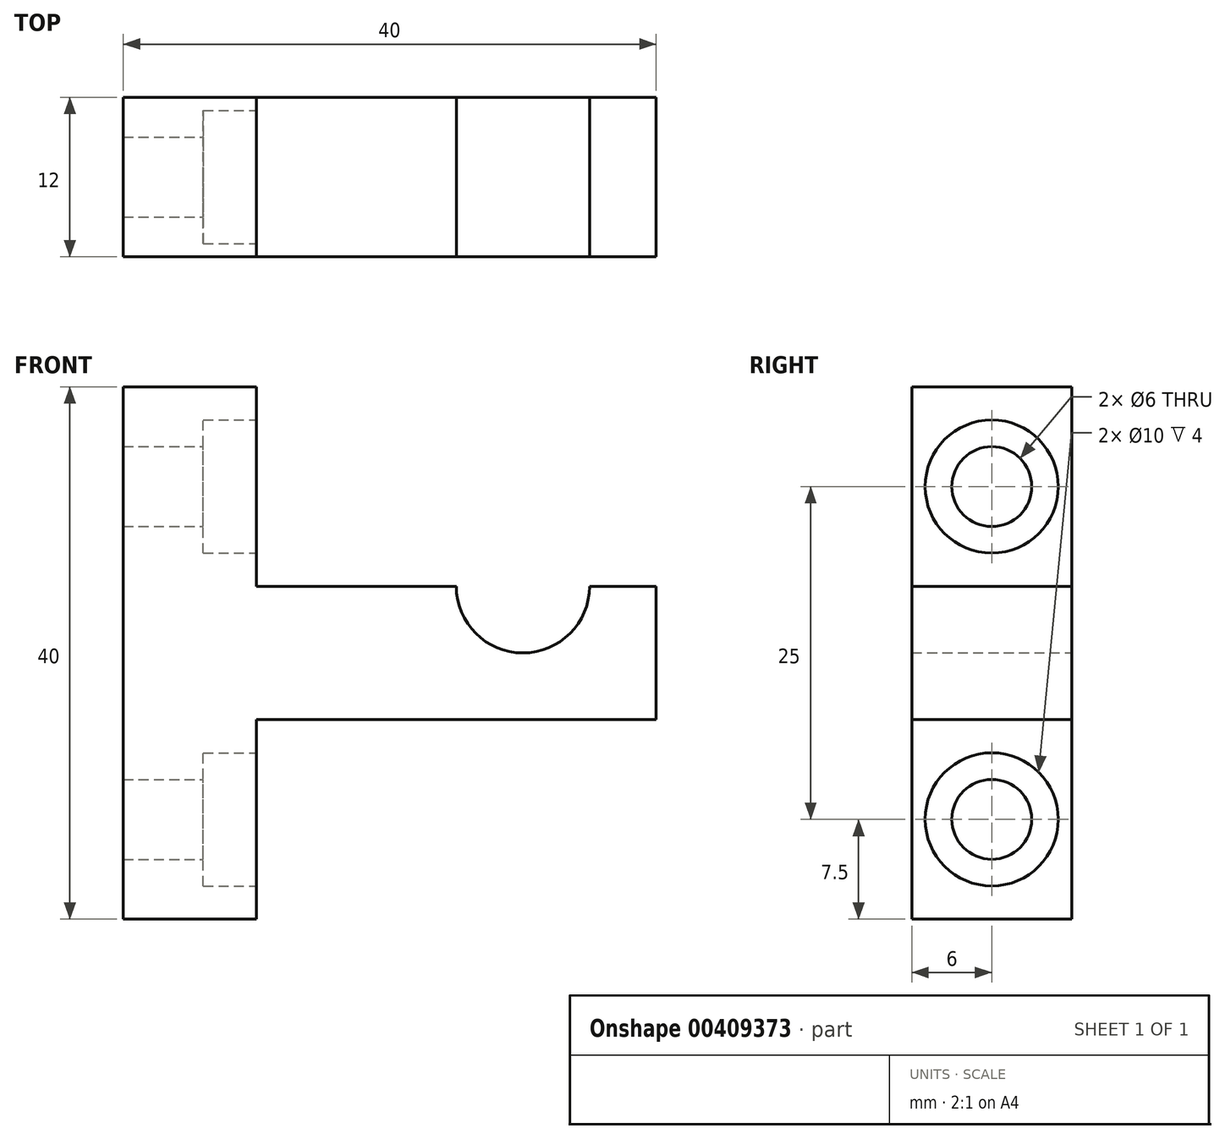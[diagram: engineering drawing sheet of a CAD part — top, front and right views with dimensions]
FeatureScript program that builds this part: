
annotation { "Feature Type Name" : "Feature", "Feature Type Description" : "" }
export const myFeature = defineFeature(function(context is Context, id is Id, definition is map)
    precondition{}
    {
        {
            var Q0;
            Q0=qCreatedBy(makeId("Front.planeOp"),FACE);
            var sketch = newSketch(context, id + "F0", { "sketchPlane" : qUnion([Q0])});
            skLineSegment(sketch, "E0.bottom", {"start": v(20, -20) * mm, "end": v(-20, -20) * mm});
            skLineSegment(sketch, "E0.top", {"start": v(20, 20) * mm, "end": v(-20, 20) * mm});
            skLineSegment(sketch, "E0.left", {"start": v(20, -20) * mm, "end": v(20, 20) * mm});
            skLineSegment(sketch, "E0.right", {"start": v(-20, -20) * mm, "end": v(-20, 20) * mm});
            skPoint(sketch, "E0.middle", {"position": v(0, 0) * mm});
            skPoint(sketch, "E1", {"position": v(10, 5) * mm});
            skCircle(sketch, "E2", {"center": v(10, 5) * mm, "radius": 5 * mm});
            skLineSegment(sketch, "E3", {"start": v(-20, 5) * mm, "end": v(20, 5) * mm});
            skLineSegment(sketch, "E4", {"start": v(-20, -5) * mm, "end": v(20, -5) * mm});
            skLineSegment(sketch, "E5", {"start": v(-10, 20) * mm, "end": v(-10, -20) * mm});
            skSolve(sketch);
        }
        {
            var Q0;
            {var subQ0=sQuery(id+"F0.wireOp",EDGE,"E0.right");var subQ1=sQuery(id+"F0.wireOp",EDGE,"E0.top");var subQ2=makeQuery(id+"F0.imprint","INTERSECT",VERTEX,{"derivedFrom":[subQ1,subQ0]});Q0=makeQuery(id+"F0.imprint","IMPRINT",FACE,{"disambiguationData":[TD([[makeQuery(id+"F0.imprint","IMPRINT",EDGE,{"disambiguationData":[TD([[subQ2,1.0]])],"derivedFrom":subQ1}),1.0]])]});}
            var Q1;
            {var subQ0=sQuery(id+"F0.wireOp",EDGE,"E3");var subQ1=sQuery(id+"F0.wireOp",EDGE,"E0.right");var subQ2=makeQuery(id+"F0.imprint","INTERSECT",VERTEX,{"derivedFrom":[subQ1,subQ0]});Q1=makeQuery(id+"F0.imprint","IMPRINT",FACE,{"disambiguationData":[TD([[makeQuery(id+"F0.imprint","IMPRINT",EDGE,{"disambiguationData":[TD([[subQ2,1.0]])],"derivedFrom":subQ1}),-1.0]])]});}
            var Q2;
            {var subQ0=sQuery(id+"F0.wireOp",EDGE,"E0.right");var subQ1=sQuery(id+"F0.wireOp",EDGE,"E0.bottom");var subQ2=makeQuery(id+"F0.imprint","INTERSECT",VERTEX,{"derivedFrom":[subQ1,subQ0]});Q2=makeQuery(id+"F0.imprint","IMPRINT",FACE,{"disambiguationData":[TD([[makeQuery(id+"F0.imprint","IMPRINT",EDGE,{"disambiguationData":[TD([[subQ2,1.0]])],"derivedFrom":subQ1}),-1.0]])]});}
            var Q3;
            {var subQ0=sQuery(id+"F0.wireOp",EDGE,"E3");var subQ6=sQuery(id+"F0.wireOp",EDGE,"E0.left");var subQ7=makeQuery(id+"F0.imprint","INTERSECT",VERTEX,{"derivedFrom":[subQ6,subQ0]});Q3=makeQuery(id+"F0.imprint","IMPRINT",FACE,{"disambiguationData":[TD([[makeQuery(id+"F0.imprint","IMPRINT",EDGE,{"disambiguationData":[TD([[subQ7,1.0]])],"derivedFrom":subQ6}),1.0]])]});}
            extrude(context, id + "F1", {"entities" : qUnion([Q0, Q1, Q2, Q3]), "depth" : 12 * mm});
        }
        {
            var Q0;
            {var subQ0=sQuery(id+"F0.wireOp",EDGE,"E5");Q0=makeQuery(id+"F1.opExtrude","SWEPT_FACE",FACE,{"disambiguationData":[OSD([subQ0]),TDD([makeQuery(id+"F0.imprint","IMPRINT",EDGE,{"disambiguationData":[TD([[makeQuery(id+"F0.imprint","INTERSECT",VERTEX,{"derivedFrom":[sQuery(id+"F0.wireOp",EDGE,"E0.top"),subQ0]}),-1.0]])],"derivedFrom":subQ0})])]});}
            var sketch = newSketch(context, id + "F2", { "sketchPlane" : qUnion([Q0])});
            skPoint(sketch, "E6", {"position": v(-6, 12.5) * mm});
            skPoint(sketch, "E6.positionSnap0", {"position": v(-6, 5) * mm});
            skPoint(sketch, "E7", {"position": v(-6, -12.5) * mm});
            skCircle(sketch, "E8", {"center": v(-6, 12.5) * mm, "radius": 3 * mm});
            skCircle(sketch, "E9", {"center": v(-6, -12.5) * mm, "radius": 3 * mm});
            skSolve(sketch);
        }
        {
            var Q0;
            Q0=makeQuery(id+"F2.imprint","IMPRINT",FACE,{"disambiguationData":[TD([[makeQuery(id+"F2.imprint","IMPRINT",EDGE,{"derivedFrom":sQuery(id+"F2.wireOp",EDGE,"E8")}),1.0]])]});
            var Q1;
            Q1=makeQuery(id+"F2.imprint","IMPRINT",FACE,{"disambiguationData":[TD([[makeQuery(id+"F2.imprint","IMPRINT",EDGE,{"derivedFrom":sQuery(id+"F2.wireOp",EDGE,"E9")}),1.0]])]});
            extrude(context, id + "F3", {"entities" : qUnion([Q0, Q1]), "operationType" : NewBodyOperationType.REMOVE, "endBound" : BoundingType.THROUGH_ALL, "oppositeDirection" : true, "depth" : 25 * mm});
        }
        {
            var Q0;
            {var subQ0=sQuery(id+"F0.wireOp",EDGE,"E5");Q0=makeQuery(id+"F1.opExtrude","SWEPT_FACE",FACE,{"disambiguationData":[OSD([subQ0]),TDD([makeQuery(id+"F0.imprint","IMPRINT",EDGE,{"disambiguationData":[TD([[makeQuery(id+"F0.imprint","INTERSECT",VERTEX,{"derivedFrom":[sQuery(id+"F0.wireOp",EDGE,"E0.top"),subQ0]}),-1.0]])],"derivedFrom":subQ0})])]});}
            var sketch = newSketch(context, id + "F4", { "sketchPlane" : qUnion([Q0])});
            skCircle(sketch, "E10", {"center": v(-6, 12.5) * mm, "radius": 5 * mm});
            skSolve(sketch);
        }
        {
            var Q0;
            Q0=makeQuery(id+"F4.imprint","IMPRINT",FACE,{"disambiguationData":[TD([[makeQuery(id+"F4.imprint","IMPRINT",EDGE,{"derivedFrom":sQuery(id+"F4.wireOp",EDGE,"E10")}),1.0]])]});
            extrude(context, id + "F5", {"entities" : qUnion([Q0]), "operationType" : NewBodyOperationType.REMOVE, "oppositeDirection" : true, "depth" : 4 * mm});
        }
        {
            var Q0;
            {var subQ0=sQuery(id+"F0.wireOp",EDGE,"E5");Q0=makeQuery(id+"F1.opExtrude","SWEPT_FACE",FACE,{"disambiguationData":[OSD([subQ0]),TDD([makeQuery(id+"F0.imprint","IMPRINT",EDGE,{"disambiguationData":[TD([[makeQuery(id+"F0.imprint","INTERSECT",VERTEX,{"derivedFrom":[sQuery(id+"F0.wireOp",EDGE,"E0.bottom"),subQ0]}),1.0]])],"derivedFrom":subQ0})])]});}
            var sketch = newSketch(context, id + "F6", { "sketchPlane" : qUnion([Q0])});
            skPoint(sketch, "E11", {"position": v(-6, -12.5) * mm});
            skCircle(sketch, "E12", {"center": v(-6, -12.5) * mm, "radius": 5 * mm});
            skSolve(sketch);
        }
        {
            var Q0;
            Q0=makeQuery(id+"F6.imprint","IMPRINT",FACE,{"disambiguationData":[TD([[makeQuery(id+"F6.imprint","IMPRINT",EDGE,{"derivedFrom":sQuery(id+"F6.wireOp",EDGE,"E12")}),1.0]])]});
            extrude(context, id + "F7", {"entities" : qUnion([Q0]), "operationType" : NewBodyOperationType.REMOVE, "oppositeDirection" : true, "depth" : 4 * mm});
        }
    });
